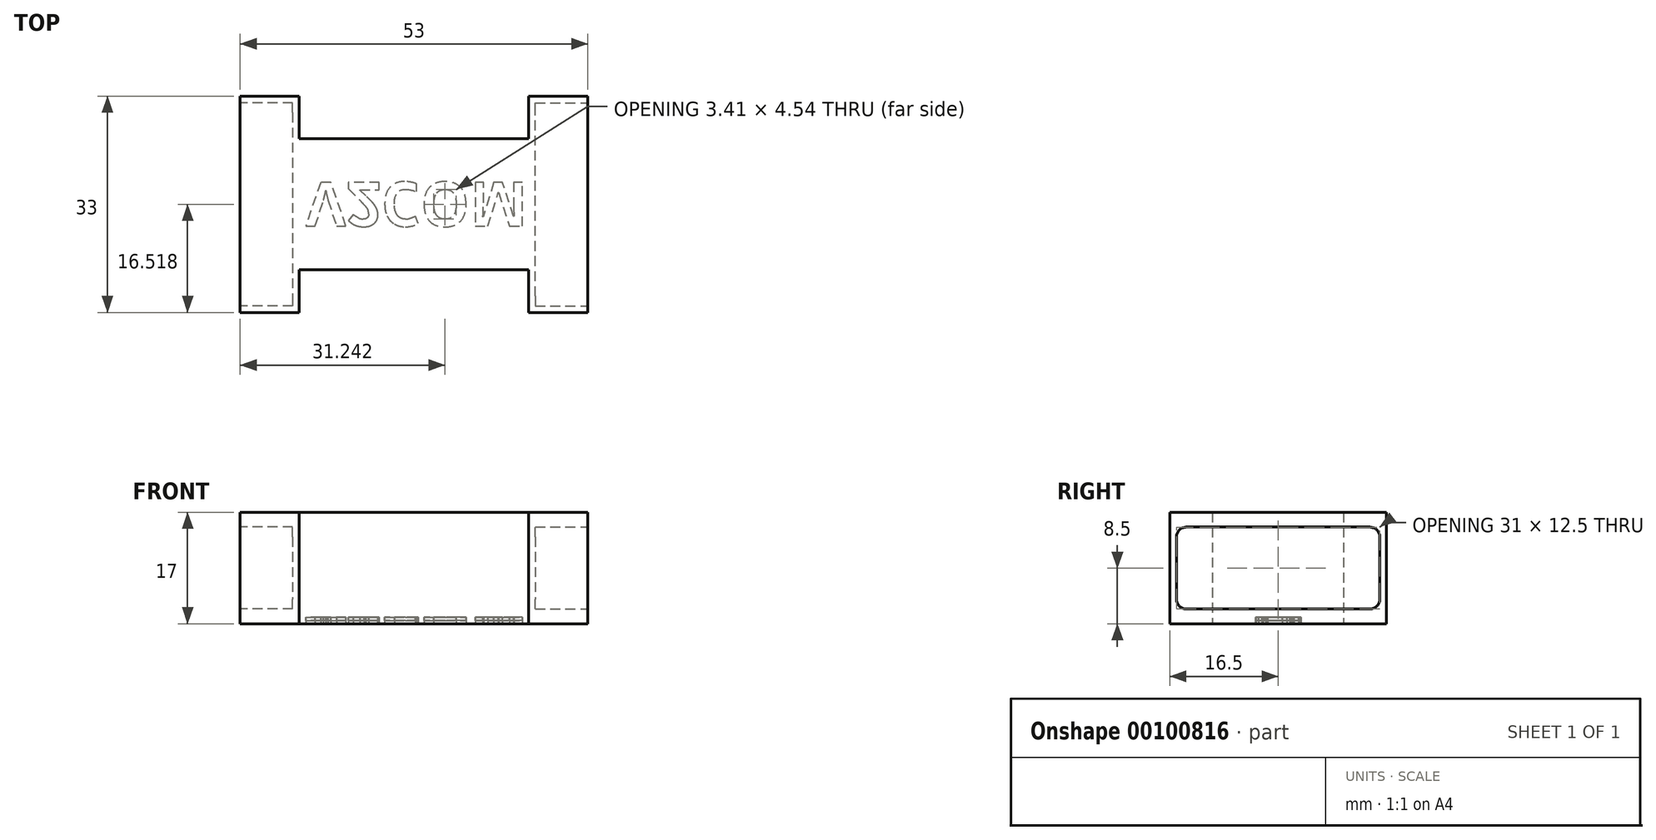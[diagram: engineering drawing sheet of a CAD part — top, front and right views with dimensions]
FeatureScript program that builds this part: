
annotation { "Feature Type Name" : "Feature", "Feature Type Description" : "" }
export const myFeature = defineFeature(function(context is Context, id is Id, definition is map)
    precondition{}
    {
        {
            var Q0;
            Q0=qCreatedBy(makeId("Top.planeOp"),FACE);
            var sketch = newSketch(context, id + "F0", { "sketchPlane" : qUnion([Q0])});
            skLineSegment(sketch, "E0", {"start": v(0, 10) * mm, "end": v(17.5, 10) * mm});
            skLineSegment(sketch, "E1", {"start": v(17.5, 10) * mm, "end": v(17.5, 16.5) * mm});
            skLineSegment(sketch, "E2", {"start": v(17.5, 16.5) * mm, "end": v(26.5, 16.5) * mm});
            skLineSegment(sketch, "E3", {"start": v(26.5, 16.5) * mm, "end": v(26.5, 0) * mm});
            skLineSegment(sketch, "E4.MirrorCS", {"start": v(26.5, -16.5) * mm, "end": v(26.5, 0) * mm});
            skLineSegment(sketch, "E5.MirrorCS", {"start": v(17.5, -10) * mm, "end": v(17.5, -16.5) * mm});
            skLineSegment(sketch, "E6.MirrorCS", {"start": v(0, -10) * mm, "end": v(17.5, -10) * mm});
            skLineSegment(sketch, "E7.MirrorCS", {"start": v(17.5, -16.5) * mm, "end": v(26.5, -16.5) * mm});
            skLineSegment(sketch, "E8.MirrorCS", {"start": v(-17.5, 16.5) * mm, "end": v(-26.5, 16.5) * mm});
            skLineSegment(sketch, "E9.MirrorCS", {"start": v(-26.5, -16.5) * mm, "end": v(-26.5, 0) * mm});
            skLineSegment(sketch, "E10.MirrorCS", {"start": v(0, -10) * mm, "end": v(-17.5, -10) * mm});
            skLineSegment(sketch, "E11.MirrorCS", {"start": v(-17.5, -16.5) * mm, "end": v(-26.5, -16.5) * mm});
            skLineSegment(sketch, "E12.MirrorCS", {"start": v(-26.5, 16.5) * mm, "end": v(-26.5, 0) * mm});
            skLineSegment(sketch, "E13.MirrorCS", {"start": v(-17.5, -10) * mm, "end": v(-17.5, -16.5) * mm});
            skLineSegment(sketch, "E14.MirrorCS", {"start": v(0, 10) * mm, "end": v(-17.5, 10) * mm});
            skLineSegment(sketch, "E15.MirrorCS", {"start": v(-17.5, 10) * mm, "end": v(-17.5, 16.5) * mm});
            skSolve(sketch);
        }
        {
            var Q0;
            Q0 = qSketchRegion(id + "F0", true);
            extrude(context, id + "F1", {"entities" : qUnion([Q0]), "endBound" : BoundingType.SYMMETRIC, "depth" : 17 * mm});
        }
        {
            var Q0;
            Q0=makeQuery(id+"F1.opExtrude","SWEPT_FACE",FACE,{"disambiguationData":[OSD([sQuery(id+"F0.wireOp",EDGE,"E9.MirrorCS"),sQuery(id+"F0.wireOp",EDGE,"E12.MirrorCS")])]});
            var sketch = newSketch(context, id + "F2", { "sketchPlane" : qUnion([Q0])});
            skLineSegment(sketch, "E16.bottom", {"start": v(-14, 6.25) * mm, "end": v(14, 6.25) * mm});
            skLineSegment(sketch, "E16.top", {"start": v(-14, -6.25) * mm, "end": v(14, -6.25) * mm});
            skLineSegment(sketch, "E16.left", {"start": v(-15.5, 4.75) * mm, "end": v(-15.5, -4.75) * mm});
            skLineSegment(sketch, "E16.right", {"start": v(15.5, 4.75) * mm, "end": v(15.5, -4.75) * mm});
            skPoint(sketch, "E16.middle", {"position": v(0, 0) * mm});
            skPoint(sketch, "E17.visualSharp", {"position": v(15.5, 6.25) * mm});
            skArc(sketch, "E17.filletArc", {"start": v(15.5, 4.75) * mm, "mid": v(15.06, 5.81) * mm, "end": v(14, 6.25) * mm});
            skPoint(sketch, "E18.visualSharp", {"position": v(15.5, -6.25) * mm});
            skArc(sketch, "E18.filletArc", {"start": v(14, -6.25) * mm, "mid": v(15.06, -5.81) * mm, "end": v(15.5, -4.75) * mm});
            skPoint(sketch, "E19.visualSharp", {"position": v(-15.5, -6.25) * mm});
            skArc(sketch, "E19.filletArc", {"start": v(-15.5, -4.75) * mm, "mid": v(-15.06, -5.81) * mm, "end": v(-14, -6.25) * mm});
            skPoint(sketch, "E20.visualSharp", {"position": v(-15.5, 6.25) * mm});
            skArc(sketch, "E20.filletArc", {"start": v(-14, 6.25) * mm, "mid": v(-15.06, 5.81) * mm, "end": v(-15.5, 4.75) * mm});
            skSolve(sketch);
        }
        {
            var Q0;
            Q0=makeQuery(id+"F2.imprint","IMPRINT",FACE,{"disambiguationData":[TD([[makeQuery(id+"F2.imprint","IMPRINT",EDGE,{"derivedFrom":sQuery(id+"F2.wireOp",EDGE,"E16.bottom")}),-1.0]])]});
            var Q1;
            Q1=makeQuery(id+"F1.opExtrude","SWEPT_FACE",FACE,{"disambiguationData":[OSD([sQuery(id+"F0.wireOp",EDGE,"E13.MirrorCS")])]});
            extrude(context, id + "F3", {"entities" : qUnion([Q0]), "operationType" : NewBodyOperationType.REMOVE, "oppositeDirection" : true, "endBoundEntityFace" : qUnion([Q1]), "depth" : 8 * mm});
        }
        {
            var Q0;
            Q0=makeQuery(id+"F1.opExtrude","SWEPT_FACE",FACE,{"disambiguationData":[OSD([sQuery(id+"F0.wireOp",EDGE,"E3"),sQuery(id+"F0.wireOp",EDGE,"E4.MirrorCS")])]});
            var sketch = newSketch(context, id + "F4", { "sketchPlane" : qUnion([Q0])});
            skLineSegment(sketch, "E21.bottom", {"start": v(-14, 6.25) * mm, "end": v(14, 6.25) * mm});
            skLineSegment(sketch, "E21.top", {"start": v(-14, -6.25) * mm, "end": v(14, -6.25) * mm});
            skLineSegment(sketch, "E21.left", {"start": v(-15.5, 4.75) * mm, "end": v(-15.5, -4.75) * mm});
            skLineSegment(sketch, "E21.right", {"start": v(15.5, 4.75) * mm, "end": v(15.5, -4.75) * mm});
            skPoint(sketch, "E21.middle", {"position": v(0, 0) * mm});
            skPoint(sketch, "E22.visualSharp", {"position": v(15.5, 6.25) * mm});
            skArc(sketch, "E22.filletArc", {"start": v(15.5, 4.75) * mm, "mid": v(15.06, 5.81) * mm, "end": v(14, 6.25) * mm});
            skPoint(sketch, "E23.visualSharp", {"position": v(15.5, -6.25) * mm});
            skArc(sketch, "E23.filletArc", {"start": v(14, -6.25) * mm, "mid": v(15.06, -5.81) * mm, "end": v(15.5, -4.75) * mm});
            skPoint(sketch, "E24.visualSharp", {"position": v(-15.5, -6.25) * mm});
            skArc(sketch, "E24.filletArc", {"start": v(-15.5, -4.75) * mm, "mid": v(-15.06, -5.81) * mm, "end": v(-14, -6.25) * mm});
            skPoint(sketch, "E25.visualSharp", {"position": v(-15.5, 6.25) * mm});
            skArc(sketch, "E25.filletArc", {"start": v(-14, 6.25) * mm, "mid": v(-15.06, 5.81) * mm, "end": v(-15.5, 4.75) * mm});
            skSolve(sketch);
        }
        {
            var Q0;
            Q0 = qSketchRegion(id + "F4", true);
            extrude(context, id + "F5", {"entities" : qUnion([Q0]), "operationType" : NewBodyOperationType.REMOVE, "oppositeDirection" : true, "depth" : 8 * mm});
        }
        {
            var Q0;
            Q0=makeQuery(id+"F1.opExtrude","CAP_FACE",FACE,{"disambiguationData":[OSD([sQuery(id+"F0.wireOp",EDGE,"E0"),sQuery(id+"F0.wireOp",EDGE,"E1"),sQuery(id+"F0.wireOp",EDGE,"E2"),sQuery(id+"F0.wireOp",EDGE,"E3"),sQuery(id+"F0.wireOp",EDGE,"E4.MirrorCS"),sQuery(id+"F0.wireOp",EDGE,"E5.MirrorCS"),sQuery(id+"F0.wireOp",EDGE,"E6.MirrorCS"),sQuery(id+"F0.wireOp",EDGE,"E7.MirrorCS"),sQuery(id+"F0.wireOp",EDGE,"E8.MirrorCS"),sQuery(id+"F0.wireOp",EDGE,"E9.MirrorCS"),sQuery(id+"F0.wireOp",EDGE,"E10.MirrorCS"),sQuery(id+"F0.wireOp",EDGE,"E11.MirrorCS"),sQuery(id+"F0.wireOp",EDGE,"E12.MirrorCS"),sQuery(id+"F0.wireOp",EDGE,"E13.MirrorCS"),sQuery(id+"F0.wireOp",EDGE,"E14.MirrorCS"),sQuery(id+"F0.wireOp",EDGE,"E15.MirrorCS")])],"isStart":true});
            var sketch = newSketch(context, id + "F6", { "sketchPlane" : qUnion([Q0])});
            skLineSegment(sketch, "E26.bottom", {"start": v(-19.54, 9.08) * mm, "end": v(19.54, 9.08) * mm, "construction": true});
            skLineSegment(sketch, "E26.top", {"start": v(-19.54, -9.08) * mm, "end": v(19.54, -9.08) * mm, "construction": true});
            skLineSegment(sketch, "E26.left", {"start": v(-19.54, 9.08) * mm, "end": v(-19.54, -9.08) * mm, "construction": true});
            skLineSegment(sketch, "E26.right", {"start": v(19.54, 9.08) * mm, "end": v(19.54, -9.08) * mm, "construction": true});
            skPoint(sketch, "E26.middle", {"position": v(0, 0) * mm});
            skLineSegment(sketch, "E27.bottom", {"start": v(-16.5, 3.39) * mm, "end": v(16.5, 3.39) * mm, "construction": true});
            skLineSegment(sketch, "E27.top", {"start": v(-16.5, -3.39) * mm, "end": v(16.5, -3.39) * mm, "construction": true});
            skLineSegment(sketch, "E27.left", {"start": v(-16.5, 3.39) * mm, "end": v(-16.5, -3.39) * mm, "construction": true});
            skLineSegment(sketch, "E27.right", {"start": v(16.5, 3.39) * mm, "end": v(16.5, -3.39) * mm, "construction": true});
            skText(sketch, "E28", { "text": "V2COM", "fontName": "OpenSans-Bold.ttf"});
            const initialGuessF6  = {"E28": [-0.0165, -0.00339, 1, 0, 0.00678]};
            skSetInitialGuess(sketch, initialGuessF6);
            skSolve(sketch);
        }
        {
            var Q0;
            Q0 = qSketchRegion(id + "F6", true);
            extrude(context, id + "F7", {"entities" : qUnion([Q0]), "operationType" : NewBodyOperationType.REMOVE, "oppositeDirection" : true, "depth" : 1 * mm});
        }
        {
            var Q0;
            Q0=makeQuery(id+"F7.boolean.opBoolean","COPY",FACE,{"derivedFrom":makeQuery(id+"F7.opExtrude","CAP_FACE",FACE,{"disambiguationData":[OSD([sQuery(id+"F6.wireOp",EDGE,"E28.sketch_text.stroke-0"),sQuery(id+"F6.wireOp",EDGE,"E28.sketch_text.stroke-1"),sQuery(id+"F6.wireOp",EDGE,"E28.sketch_text.stroke-2"),sQuery(id+"F6.wireOp",EDGE,"E28.sketch_text.stroke-3"),sQuery(id+"F6.wireOp",EDGE,"E28.sketch_text.stroke-4"),sQuery(id+"F6.wireOp",EDGE,"E28.sketch_text.stroke-5"),sQuery(id+"F6.wireOp",EDGE,"E28.sketch_text.stroke-6"),sQuery(id+"F6.wireOp",EDGE,"E28.sketch_text.stroke-7"),sQuery(id+"F6.wireOp",EDGE,"E28.sketch_text.stroke-8"),sQuery(id+"F6.wireOp",EDGE,"E28.sketch_text.stroke-9")])],"isStart":false})});
            var Q1;
            Q1=makeQuery(id+"F7.boolean.opBoolean","COPY",FACE,{"derivedFrom":makeQuery(id+"F7.opExtrude","CAP_FACE",FACE,{"disambiguationData":[OSD([sQuery(id+"F6.wireOp",EDGE,"E28.sketch_text.stroke-10"),sQuery(id+"F6.wireOp",EDGE,"E28.sketch_text.stroke-11"),sQuery(id+"F6.wireOp",EDGE,"E28.sketch_text.stroke-12"),sQuery(id+"F6.wireOp",EDGE,"E28.sketch_text.stroke-13"),sQuery(id+"F6.wireOp",EDGE,"E28.sketch_text.stroke-14"),sQuery(id+"F6.wireOp",EDGE,"E28.sketch_text.stroke-15"),sQuery(id+"F6.wireOp",EDGE,"E28.sketch_text.stroke-16"),sQuery(id+"F6.wireOp",EDGE,"E28.sketch_text.stroke-17"),sQuery(id+"F6.wireOp",EDGE,"E28.sketch_text.stroke-18"),sQuery(id+"F6.wireOp",EDGE,"E28.sketch_text.stroke-19"),sQuery(id+"F6.wireOp",EDGE,"E28.sketch_text.stroke-20"),sQuery(id+"F6.wireOp",EDGE,"E28.sketch_text.stroke-21"),sQuery(id+"F6.wireOp",EDGE,"E28.sketch_text.stroke-22"),sQuery(id+"F6.wireOp",EDGE,"E28.sketch_text.stroke-23"),sQuery(id+"F6.wireOp",EDGE,"E28.sketch_text.stroke-24"),sQuery(id+"F6.wireOp",EDGE,"E28.sketch_text.stroke-25"),sQuery(id+"F6.wireOp",EDGE,"E28.sketch_text.stroke-26"),sQuery(id+"F6.wireOp",EDGE,"E28.sketch_text.stroke-27"),sQuery(id+"F6.wireOp",EDGE,"E28.sketch_text.stroke-28"),sQuery(id+"F6.wireOp",EDGE,"E28.sketch_text.stroke-29"),sQuery(id+"F6.wireOp",EDGE,"E28.sketch_text.stroke-30"),sQuery(id+"F6.wireOp",EDGE,"E28.sketch_text.stroke-31"),sQuery(id+"F6.wireOp",EDGE,"E28.sketch_text.stroke-32"),sQuery(id+"F6.wireOp",EDGE,"E28.sketch_text.stroke-33")])],"isStart":false})});
            var Q2;
            Q2=makeQuery(id+"F7.boolean.opBoolean","COPY",FACE,{"derivedFrom":makeQuery(id+"F7.opExtrude","CAP_FACE",FACE,{"disambiguationData":[OSD([sQuery(id+"F6.wireOp",EDGE,"E28.sketch_text.stroke-34"),sQuery(id+"F6.wireOp",EDGE,"E28.sketch_text.stroke-35"),sQuery(id+"F6.wireOp",EDGE,"E28.sketch_text.stroke-36"),sQuery(id+"F6.wireOp",EDGE,"E28.sketch_text.stroke-37"),sQuery(id+"F6.wireOp",EDGE,"E28.sketch_text.stroke-38"),sQuery(id+"F6.wireOp",EDGE,"E28.sketch_text.stroke-39"),sQuery(id+"F6.wireOp",EDGE,"E28.sketch_text.stroke-40"),sQuery(id+"F6.wireOp",EDGE,"E28.sketch_text.stroke-41"),sQuery(id+"F6.wireOp",EDGE,"E28.sketch_text.stroke-42"),sQuery(id+"F6.wireOp",EDGE,"E28.sketch_text.stroke-43"),sQuery(id+"F6.wireOp",EDGE,"E28.sketch_text.stroke-44"),sQuery(id+"F6.wireOp",EDGE,"E28.sketch_text.stroke-45"),sQuery(id+"F6.wireOp",EDGE,"E28.sketch_text.stroke-46"),sQuery(id+"F6.wireOp",EDGE,"E28.sketch_text.stroke-47"),sQuery(id+"F6.wireOp",EDGE,"E28.sketch_text.stroke-48")])],"isStart":false})});
            var Q3;
            Q3=makeQuery(id+"F7.boolean.opBoolean","COPY",FACE,{"derivedFrom":makeQuery(id+"F7.opExtrude","CAP_FACE",FACE,{"disambiguationData":[OSD([sQuery(id+"F6.wireOp",EDGE,"E28.sketch_text.stroke-49"),sQuery(id+"F6.wireOp",EDGE,"E28.sketch_text.stroke-50"),sQuery(id+"F6.wireOp",EDGE,"E28.sketch_text.stroke-51"),sQuery(id+"F6.wireOp",EDGE,"E28.sketch_text.stroke-52"),sQuery(id+"F6.wireOp",EDGE,"E28.sketch_text.stroke-53"),sQuery(id+"F6.wireOp",EDGE,"E28.sketch_text.stroke-54"),sQuery(id+"F6.wireOp",EDGE,"E28.sketch_text.stroke-55"),sQuery(id+"F6.wireOp",EDGE,"E28.sketch_text.stroke-56"),sQuery(id+"F6.wireOp",EDGE,"E28.sketch_text.stroke-57"),sQuery(id+"F6.wireOp",EDGE,"E28.sketch_text.stroke-58"),sQuery(id+"F6.wireOp",EDGE,"E28.sketch_text.stroke-59"),sQuery(id+"F6.wireOp",EDGE,"E28.sketch_text.stroke-60"),sQuery(id+"F6.wireOp",EDGE,"E28.sketch_text.stroke-61"),sQuery(id+"F6.wireOp",EDGE,"E28.sketch_text.stroke-62")])],"isStart":false})});
            var Q4;
            Q4=makeQuery(id+"F7.boolean.opBoolean","COPY",FACE,{"derivedFrom":makeQuery(id+"F7.opExtrude","CAP_FACE",FACE,{"disambiguationData":[OSD([sQuery(id+"F6.wireOp",EDGE,"E28.sketch_text.stroke-63"),sQuery(id+"F6.wireOp",EDGE,"E28.sketch_text.stroke-64"),sQuery(id+"F6.wireOp",EDGE,"E28.sketch_text.stroke-65"),sQuery(id+"F6.wireOp",EDGE,"E28.sketch_text.stroke-66"),sQuery(id+"F6.wireOp",EDGE,"E28.sketch_text.stroke-67"),sQuery(id+"F6.wireOp",EDGE,"E28.sketch_text.stroke-68"),sQuery(id+"F6.wireOp",EDGE,"E28.sketch_text.stroke-69"),sQuery(id+"F6.wireOp",EDGE,"E28.sketch_text.stroke-70"),sQuery(id+"F6.wireOp",EDGE,"E28.sketch_text.stroke-71"),sQuery(id+"F6.wireOp",EDGE,"E28.sketch_text.stroke-72"),sQuery(id+"F6.wireOp",EDGE,"E28.sketch_text.stroke-73"),sQuery(id+"F6.wireOp",EDGE,"E28.sketch_text.stroke-74"),sQuery(id+"F6.wireOp",EDGE,"E28.sketch_text.stroke-75"),sQuery(id+"F6.wireOp",EDGE,"E28.sketch_text.stroke-76"),sQuery(id+"F6.wireOp",EDGE,"E28.sketch_text.stroke-77"),sQuery(id+"F6.wireOp",EDGE,"E28.sketch_text.stroke-78"),sQuery(id+"F6.wireOp",EDGE,"E28.sketch_text.stroke-79"),sQuery(id+"F6.wireOp",EDGE,"E28.sketch_text.stroke-80"),sQuery(id+"F6.wireOp",EDGE,"E28.sketch_text.stroke-81")])],"isStart":false})});
            extrude(context, id + "F8", {"entities" : qUnion([Q0, Q1, Q2, Q3, Q4]), "depth" : 0.5 * mm});
        }
    });
